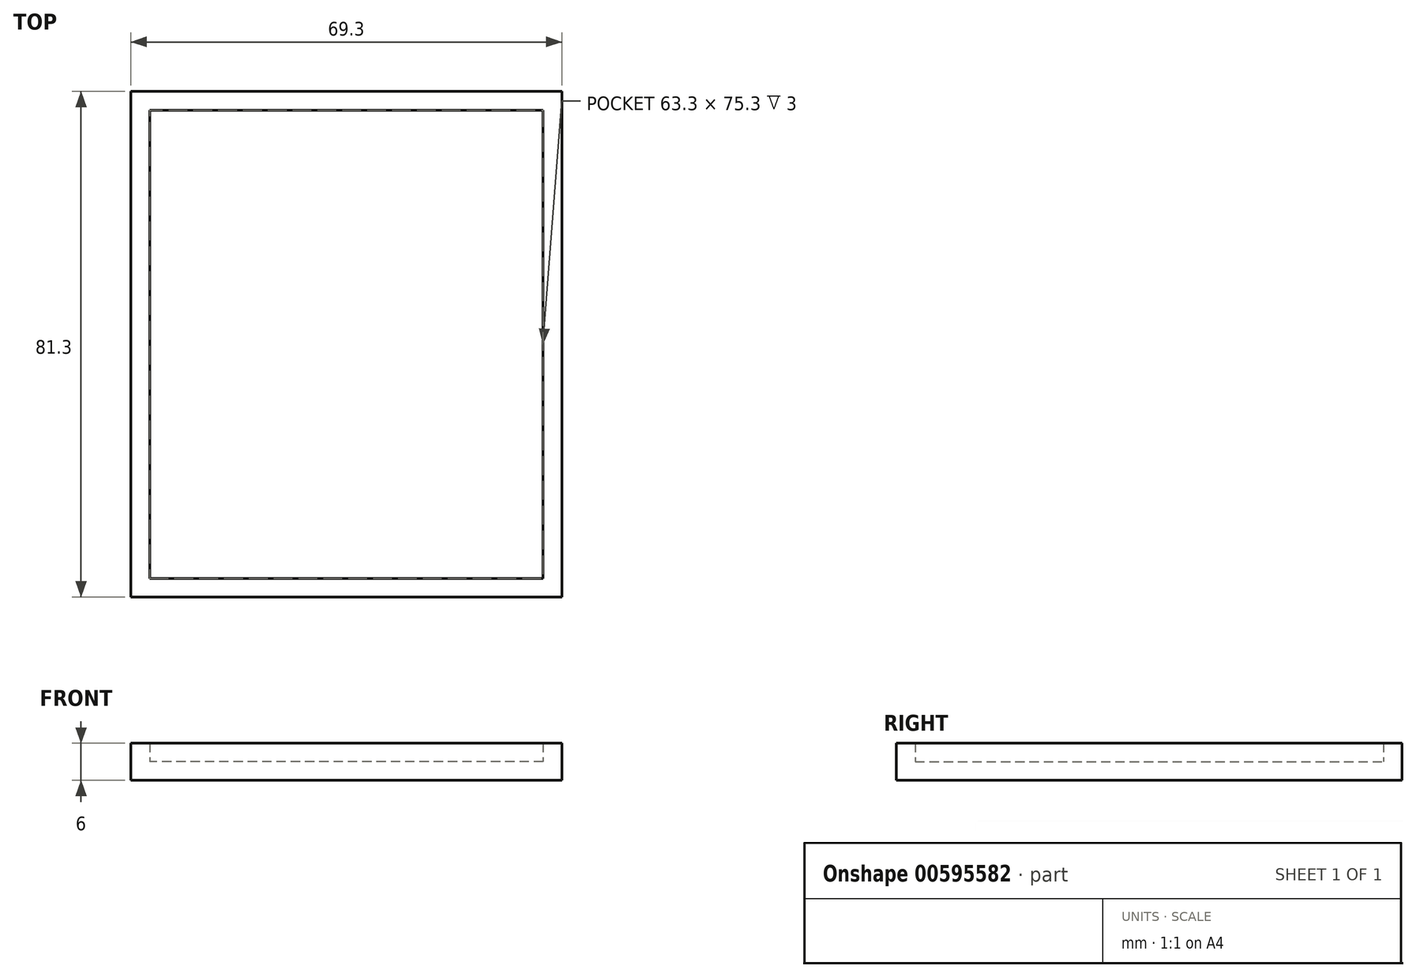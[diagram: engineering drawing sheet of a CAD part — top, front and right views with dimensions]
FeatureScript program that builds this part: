
annotation { "Feature Type Name" : "Feature", "Feature Type Description" : "" }
export const myFeature = defineFeature(function(context is Context, id is Id, definition is map)
    precondition{}
    {
        {
            var Q0;
            Q0=qCreatedBy(makeId("Top.planeOp"),FACE);
            var sketch = newSketch(context, id + "F0", { "sketchPlane" : qUnion([Q0])});
            skPoint(sketch, "E0.middle", {"position": v(0, 0) * mm});
            skLineSegment(sketch, "E1.0", {"start": v(34.65, 40.65) * mm, "end": v(-34.65, 40.65) * mm});
            skLineSegment(sketch, "E1.1", {"start": v(34.65, -40.65) * mm, "end": v(34.65, 40.65) * mm});
            skLineSegment(sketch, "E1.2", {"start": v(34.65, -40.65) * mm, "end": v(-34.65, -40.65) * mm});
            skLineSegment(sketch, "E1.3", {"start": v(-34.65, -40.65) * mm, "end": v(-34.65, 40.65) * mm});
            skPoint(sketch, "E0.left.end.orphan", {"position": v(31.65, 37.65) * mm});
            skPoint(sketch, "E0.bottom.start.orphan", {"position": v(31.65, -37.65) * mm});
            skPoint(sketch, "E0.right.end.orphan", {"position": v(-31.65, 37.65) * mm});
            skPoint(sketch, "E0.right.start.orphan", {"position": v(-31.65, -37.65) * mm});
            skSolve(sketch);
        }
        {
            var Q0;
            Q0 = qSketchRegion(id + "F0", true);
            extrude(context, id + "F1", {"entities" : qUnion([Q0]), "depth" : 6 * mm, "offsetDistance" : 25 * mm});
        }
        {
            var Q0;
            Q0=makeQuery(id+"F1.opExtrude","CAP_FACE",FACE,{"disambiguationData":[OSD([sQuery(id+"F0.wireOp",EDGE,"E1.0"),sQuery(id+"F0.wireOp",EDGE,"E1.1"),sQuery(id+"F0.wireOp",EDGE,"E1.2"),sQuery(id+"F0.wireOp",EDGE,"E1.3")])],"isStart":false});
            shell(context, id + "F2", {"entities" : qUnion([Q0]), "thickness" : 3 * mm});
        }
    });
